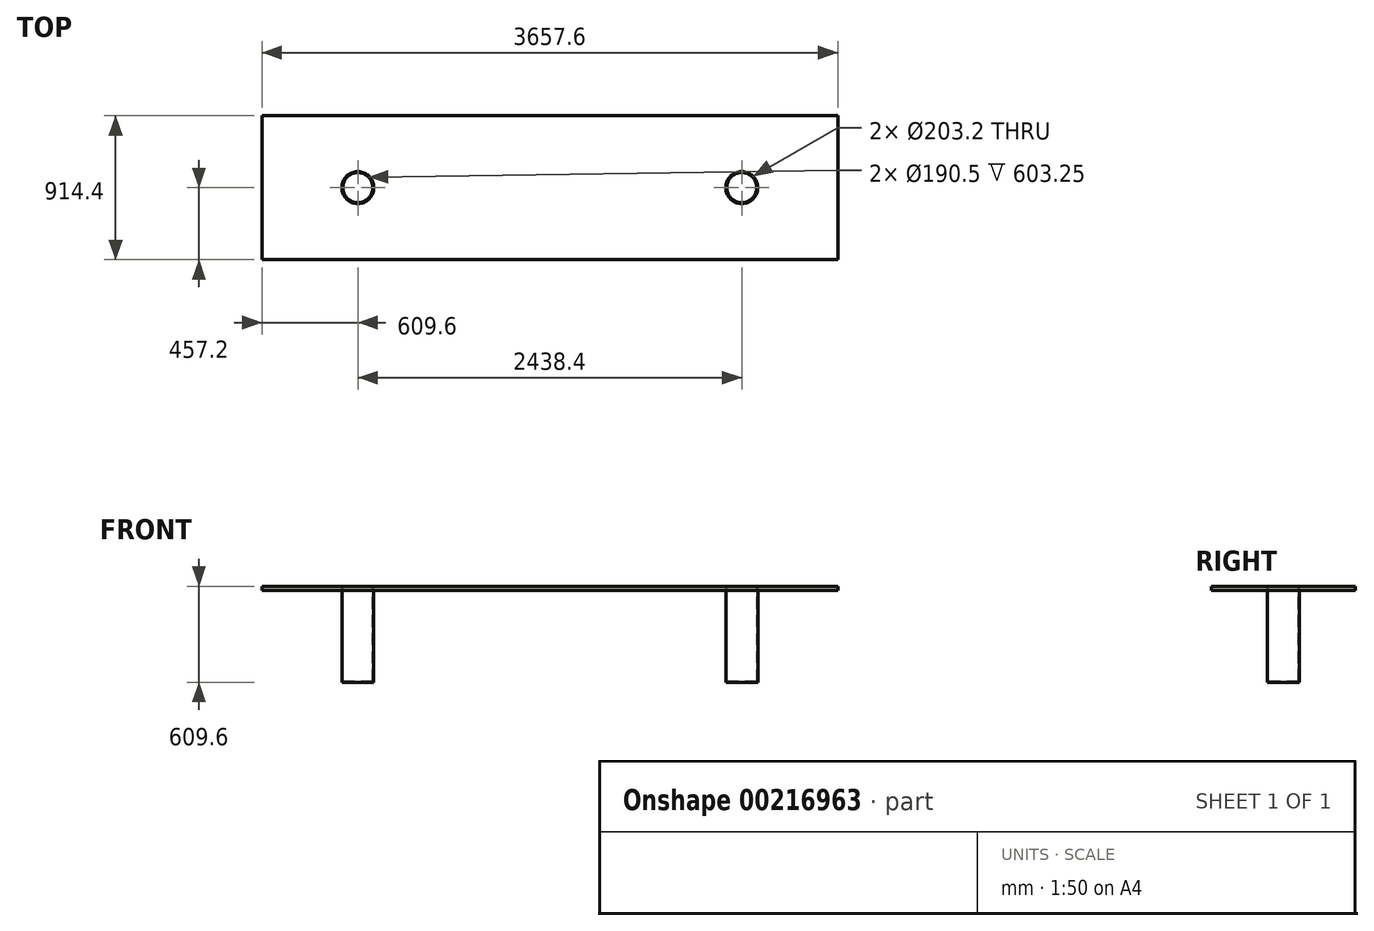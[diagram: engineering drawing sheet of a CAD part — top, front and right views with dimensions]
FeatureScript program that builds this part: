
annotation { "Feature Type Name" : "Feature", "Feature Type Description" : "" }
export const myFeature = defineFeature(function(context is Context, id is Id, definition is map)
    precondition{}
    {
        {
            var Q0;
            Q0=qCreatedBy(makeId("Top.planeOp"),FACE);
            var sketch = newSketch(context, id + "F0", { "sketchPlane" : qUnion([Q0])});
            skCircle(sketch, "E0", {"center": v(0, 0) * mm, "radius": 101.6 * mm});
            skCircle(sketch, "E1", {"center": v(2438.4, 0) * mm, "radius": 101.6 * mm});
            skSolve(sketch);
        }
        {
            var Q0;
            Q0 = qSketchRegion(id + "F0", true);
            extrude(context, id + "F1", {"entities" : qUnion([Q0]), "oppositeDirection" : true, "depth" : 609.6 * mm, "offsetDistance" : 25.4 * mm});
        }
        {
            var Q0;
            Q0=makeQuery(id+"F1.opExtrude","CAP_FACE",FACE,{"disambiguationData":[OSD([sQuery(id+"F0.wireOp",EDGE,"E0")])],"isStart":true});
            var Q1;
            Q1=makeQuery(id+"F1.opExtrude","CAP_FACE",FACE,{"disambiguationData":[OSD([sQuery(id+"F0.wireOp",EDGE,"E1")])],"isStart":true});
            shell(context, id + "F2", {"entities" : qUnion([Q0, Q1]), "thickness" : 6.35 * mm});
        }
        {
            var Q0;
            Q0=makeQuery(id+"F1.opExtrude","CAP_FACE",FACE,{"disambiguationData":[OSD([sQuery(id+"F0.wireOp",EDGE,"E0")])],"isStart":true});
            var sketch = newSketch(context, id + "F3", { "sketchPlane" : qUnion([Q0])});
            skLineSegment(sketch, "E2.bottom", {"start": v(3048, 457.2) * mm, "end": v(-609.6, 457.2) * mm});
            skLineSegment(sketch, "E2.top", {"start": v(3048, -457.2) * mm, "end": v(-609.6, -457.2) * mm});
            skLineSegment(sketch, "E2.left", {"start": v(3048, 457.2) * mm, "end": v(3048, -457.2) * mm});
            skLineSegment(sketch, "E2.right", {"start": v(-609.6, 457.2) * mm, "end": v(-609.6, -457.2) * mm});
            skPoint(sketch, "E2.middle", {"position": v(1219.2, 0) * mm});
            skCircle(sketch, "E3", {"center": v(0, 0) * mm, "radius": 101.6 * mm});
            skCircle(sketch, "E4", {"center": v(2438.4, 0) * mm, "radius": 101.6 * mm});
            skSolve(sketch);
        }
        {
            var Q0;
            Q0 = qSketchRegion(id + "F3", true);
            extrude(context, id + "F4", {"entities" : qUnion([Q0]), "oppositeDirection" : true, "depth" : 25.4 * mm, "offsetDistance" : 25.4 * mm});
        }
    });
